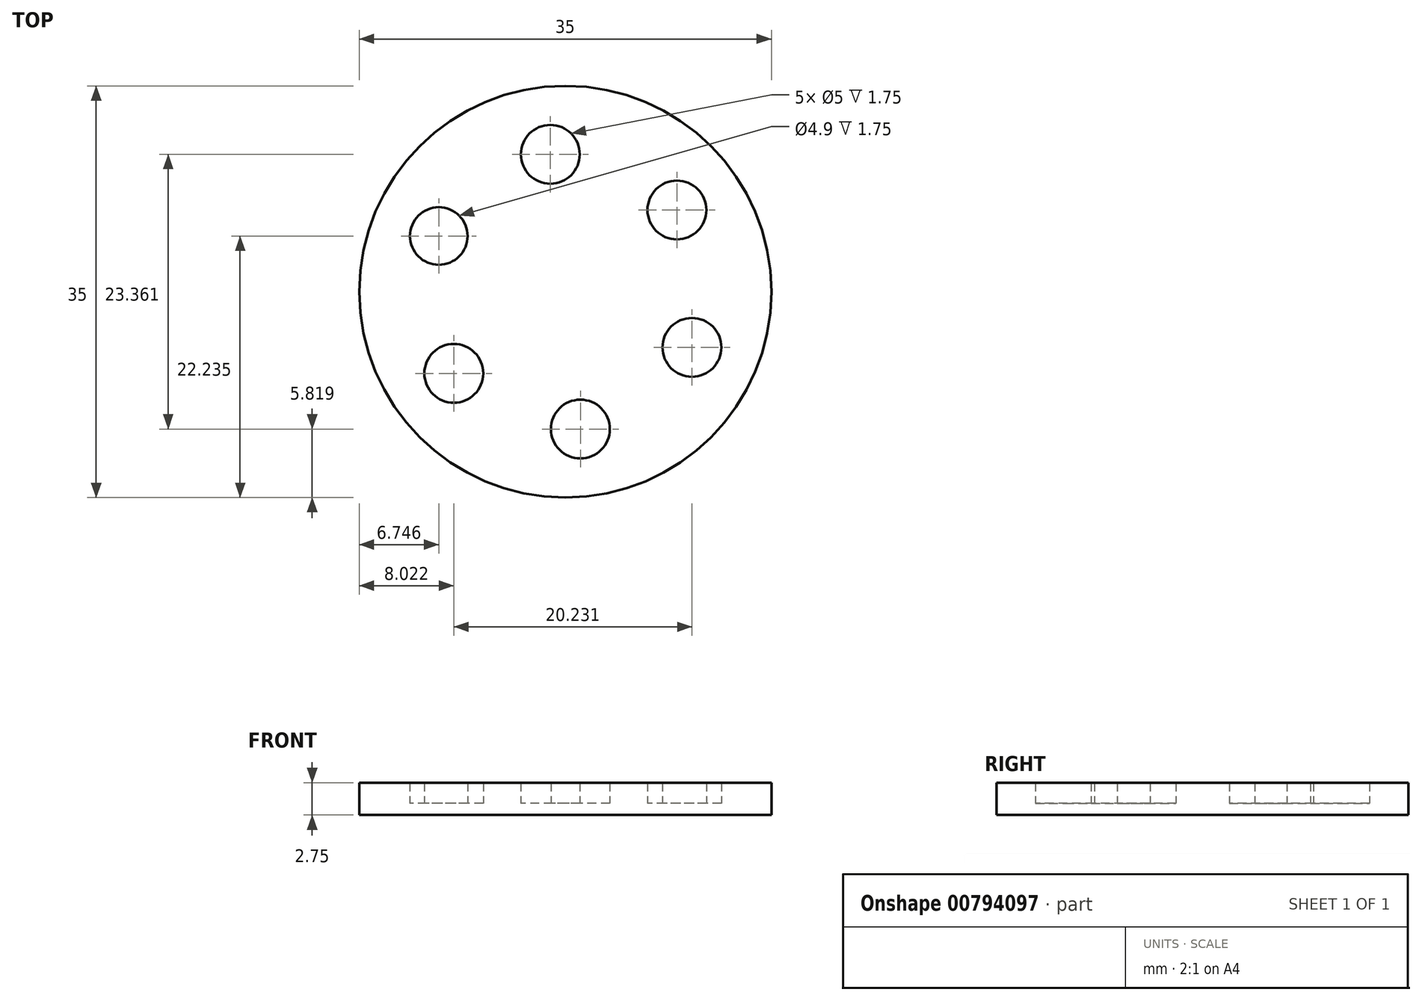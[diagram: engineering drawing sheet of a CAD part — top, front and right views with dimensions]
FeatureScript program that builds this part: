
annotation { "Feature Type Name" : "Feature", "Feature Type Description" : "" }
export const myFeature = defineFeature(function(context is Context, id is Id, definition is map)
    precondition{}
    {
        {
            var Q0;
            Q0=qCreatedBy(makeId("Top.planeOp"),FACE);
            var sketch = newSketch(context, id + "F0", { "sketchPlane" : qUnion([Q0])});
            skCircle(sketch, "E0", {"center": v(0, 0) * mm, "radius": 17.5 * mm});
            skSolve(sketch);
        }
        {
            var Q0;
            Q0=makeQuery(id+"F0.imprint","IMPRINT",FACE,{"disambiguationData":[TD([[makeQuery(id+"F0.imprint","IMPRINT",EDGE,{"derivedFrom":sQuery(id+"F0.wireOp",EDGE,"E0")}),1.0]])]});
            extrude(context, id + "F1", {"entities" : qUnion([Q0]), "depth" : 1 * mm, "offsetDistance" : 25 * mm});
        }
        {
            var Q0;
            Q0=makeQuery(id+"F1.opExtrude","CAP_FACE",FACE,{"disambiguationData":[OSD([sQuery(id+"F0.wireOp",EDGE,"E0")])],"isStart":false});
            var sketch = newSketch(context, id + "F2", { "sketchPlane" : qUnion([Q0])});
            skCircle(sketch, "E1", {"center": v(-1.28, 11.68) * mm, "radius": 2.5 * mm});
            skCircle(sketch, "E2", {"center": v(9.48, 6.95) * mm, "radius": 2.5 * mm});
            skCircle(sketch, "E3", {"center": v(1.28, -11.68) * mm, "radius": 2.5 * mm});
            skCircle(sketch, "E4", {"center": v(-9.48, -6.95) * mm, "radius": 2.5 * mm});
            skCircle(sketch, "E5", {"center": v(-10.75, 4.74) * mm, "radius": 2.45 * mm});
            skCircle(sketch, "E6", {"center": v(10.75, -4.74) * mm, "radius": 2.5 * mm});
            skSolve(sketch);
        }
        {
            var Q0;
            Q0=makeQuery(id+"F2.imprint","IMPRINT",FACE,{"disambiguationData":[TD([[makeQuery(id+"F2.imprint","IMPRINT",EDGE,{"derivedFrom":sQuery(id+"F2.wireOp",EDGE,"E1")}),-1.0]])]});
            extrude(context, id + "F3", {"entities" : qUnion([Q0]), "operationType" : NewBodyOperationType.ADD, "depth" : 1.75 * mm, "offsetDistance" : 25 * mm});
        }
    });
